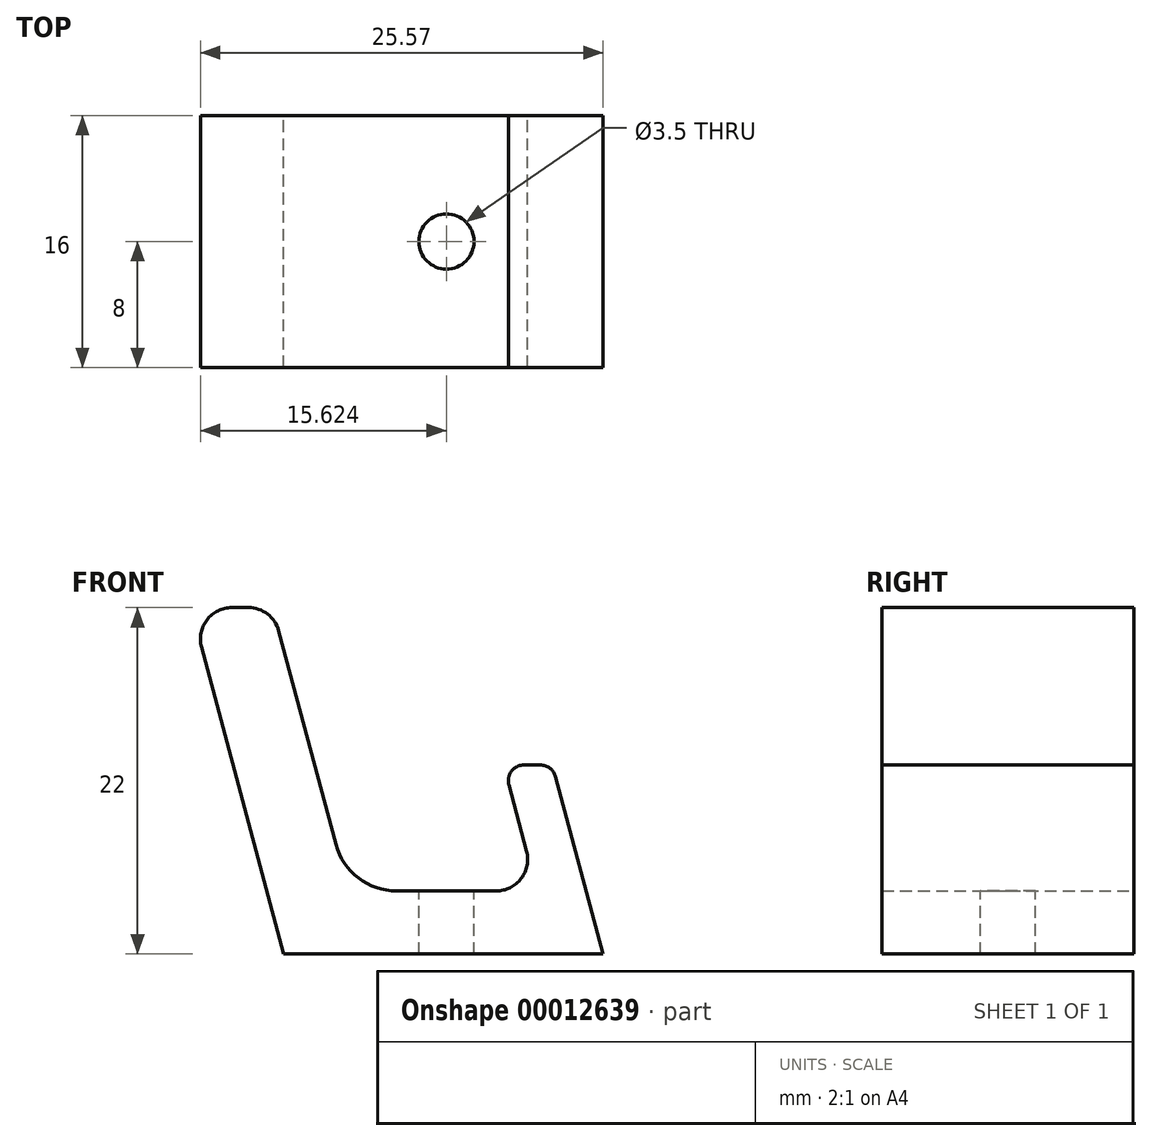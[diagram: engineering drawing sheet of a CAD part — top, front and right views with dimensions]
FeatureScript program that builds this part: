
annotation { "Feature Type Name" : "Feature", "Feature Type Description" : "" }
export const myFeature = defineFeature(function(context is Context, id is Id, definition is map)
    precondition{}
    {
        {
            var Q0;
            Q0=qCreatedBy(makeId("Front.planeOp"),FACE);
            var sketch = newSketch(context, id + "F0", { "sketchPlane" : qUnion([Q0])});
            skLineSegment(sketch, "E0", {"start": v(0, 0) * mm, "end": v(-20.28, 0) * mm});
            skLineSegment(sketch, "E1", {"start": v(-20.28, 0) * mm, "end": v(-25.5, 19.48) * mm});
            skLineSegment(sketch, "E2", {"start": v(-23.57, 22) * mm, "end": v(-22.54, 22) * mm});
            skLineSegment(sketch, "E3", {"start": v(-20.6, 20.52) * mm, "end": v(-16.97, 6.96) * mm});
            skLineSegment(sketch, "E4", {"start": v(-13.1, 4) * mm, "end": v(-6.78, 4) * mm});
            skLineSegment(sketch, "E5", {"start": v(-4.85, 6.52) * mm, "end": v(-5.98, 10.74) * mm});
            skLineSegment(sketch, "E6", {"start": v(-5.02, 12) * mm, "end": v(-3.98, 12) * mm});
            skLineSegment(sketch, "E7", {"start": v(-3.02, 11.26) * mm, "end": v(0, 0) * mm});
            skPoint(sketch, "E8.visualSharp", {"position": v(-16.18, 4) * mm});
            skArc(sketch, "E8.filletArc", {"start": v(-16.97, 6.96) * mm, "mid": v(-15.54, 4.83) * mm, "end": v(-13.1, 4) * mm});
            skPoint(sketch, "E9.visualSharp", {"position": v(-21, 22) * mm});
            skArc(sketch, "E9.filletArc", {"start": v(-20.6, 20.52) * mm, "mid": v(-21.32, 21.59) * mm, "end": v(-22.54, 22) * mm});
            skPoint(sketch, "E10.visualSharp", {"position": v(-26.18, 22) * mm});
            skArc(sketch, "E10.filletArc", {"start": v(-23.57, 22) * mm, "mid": v(-25.16, 21.22) * mm, "end": v(-25.5, 19.48) * mm});
            skPoint(sketch, "E11.visualSharp", {"position": v(-4.18, 4) * mm});
            skArc(sketch, "E11.filletArc", {"start": v(-6.78, 4) * mm, "mid": v(-5.2, 4.78) * mm, "end": v(-4.85, 6.52) * mm});
            skPoint(sketch, "E12.visualSharp", {"position": v(-6.32, 12) * mm});
            skArc(sketch, "E12.filletArc", {"start": v(-5.02, 12) * mm, "mid": v(-5.81, 11.6) * mm, "end": v(-5.98, 10.74) * mm});
            skPoint(sketch, "E13.visualSharp", {"position": v(-3.22, 12) * mm});
            skArc(sketch, "E13.filletArc", {"start": v(-3.02, 11.26) * mm, "mid": v(-3.37, 11.8) * mm, "end": v(-3.98, 12) * mm});
            skSolve(sketch);
        }
        {
            var Q0;
            Q0 = qSketchRegion(id + "F0", true);
            extrude(context, id + "F1", {"entities" : qUnion([Q0]), "depth" : 8 * mm, "hasSecondDirection" : true, "secondDirectionOppositeDirection" : true, "secondDirectionDepth" : 8 * mm});
        }
        {
            var Q0;
            Q0=makeQuery(id+"F1.opExtrude","SWEPT_FACE",FACE,{"disambiguationData":[OSD([sQuery(id+"F0.wireOp",EDGE,"E4")])]});
            var sketch = newSketch(context, id + "F2", { "sketchPlane" : qUnion([Q0])});
            skCircle(sketch, "E14", {"center": v(-9.95, 0) * mm, "radius": 1.75 * mm});
            skLineSegment(sketch, "E15", {"start": v(-13.1, 0) * mm, "end": v(-6.78, 0) * mm, "construction": true});
            skSolve(sketch);
        }
        {
            var Q0;
            Q0 = qSketchRegion(id + "F2", true);
            extrude(context, id + "F3", {"entities" : qUnion([Q0]), "operationType" : NewBodyOperationType.REMOVE, "endBound" : BoundingType.UP_TO_NEXT, "oppositeDirection" : true, "depth" : 25 * mm});
        }
    });
